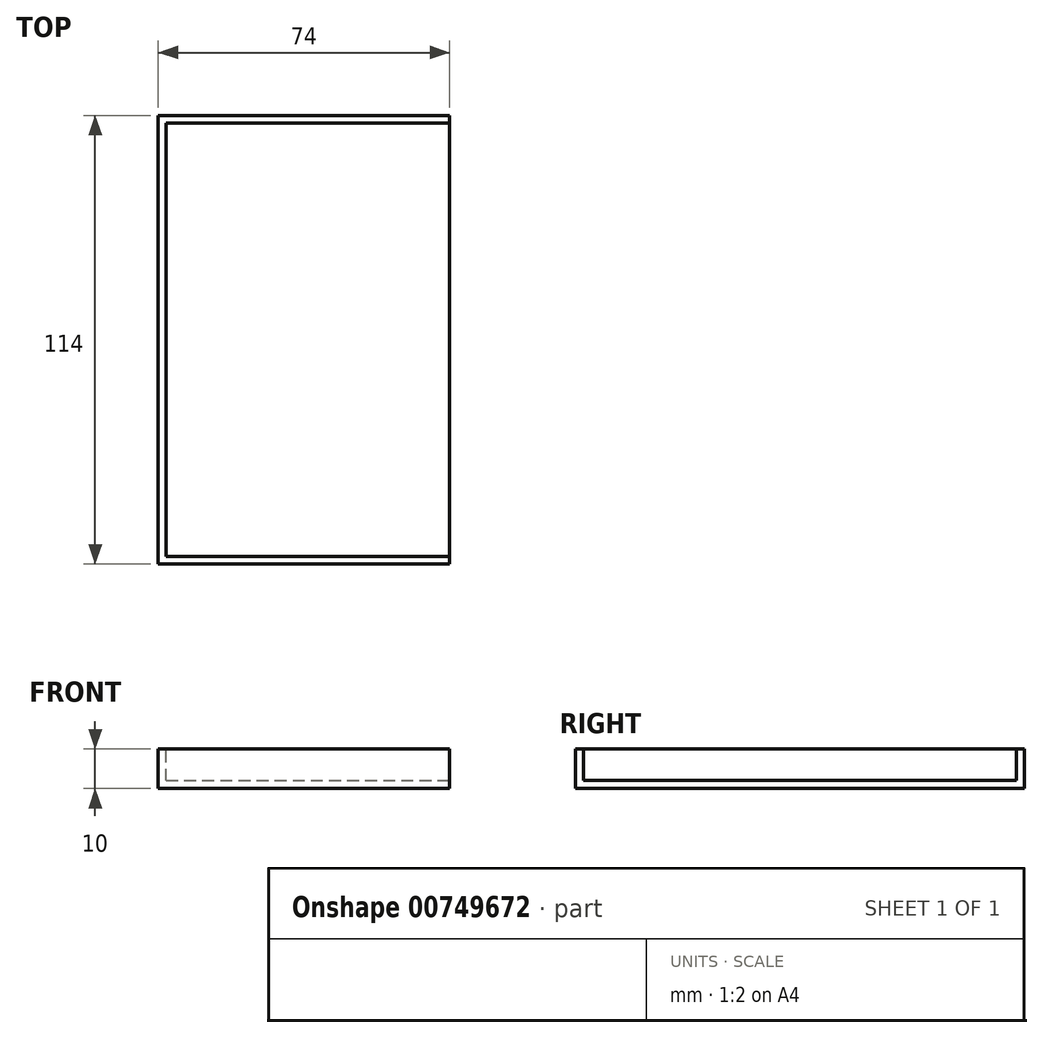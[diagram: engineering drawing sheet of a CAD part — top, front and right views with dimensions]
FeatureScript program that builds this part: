
annotation { "Feature Type Name" : "Feature", "Feature Type Description" : "" }
export const myFeature = defineFeature(function(context is Context, id is Id, definition is map)
    precondition{}
    {
        {
            var Q0;
            Q0=qCreatedBy(makeId("Top.planeOp"),FACE);
            var sketch = newSketch(context, id + "F0", { "sketchPlane" : qUnion([Q0])});
            skLineSegment(sketch, "E0.bottom", {"start": v(-89.45, 57) * mm, "end": v(-15.45, 57) * mm});
            skLineSegment(sketch, "E0.top", {"start": v(-89.45, -57) * mm, "end": v(-15.45, -57) * mm});
            skLineSegment(sketch, "E0.left", {"start": v(-89.45, 57) * mm, "end": v(-89.45, -57) * mm});
            skLineSegment(sketch, "E0.right", {"start": v(-15.45, 57) * mm, "end": v(-15.45, -57) * mm});
            skSolve(sketch);
        }
        {
            var Q0;
            Q0=qSketchRegion(id+"F0",true);
            extrude(context, id + "F1", {"entities" : qUnion([Q0]), "depth" : 10 * mm, "offsetDistance" : 25 * mm});
        }
        {
            var Q0;
            Q0=makeQuery(id+"F1.opExtrude","CAP_FACE",FACE,{"disambiguationData":[OSD([sQuery(id+"F0.wireOp",EDGE,"E0.bottom"),sQuery(id+"F0.wireOp",EDGE,"E0.top"),sQuery(id+"F0.wireOp",EDGE,"E0.left"),sQuery(id+"F0.wireOp",EDGE,"E0.right")])],"isStart":false});
            var sketch = newSketch(context, id + "F2", { "sketchPlane" : qUnion([Q0])});
            skLineSegment(sketch, "E1.0", {"start": v(-89.45, 57) * mm, "end": v(-15.45, 57) * mm, "construction": true});
            skLineSegment(sketch, "E1.1", {"start": v(-89.45, 57) * mm, "end": v(-89.45, -57) * mm, "construction": true});
            skLineSegment(sketch, "E1.2", {"start": v(-15.45, 57) * mm, "end": v(-15.45, -57) * mm, "construction": true});
            skLineSegment(sketch, "E1.3", {"start": v(-89.45, -57) * mm, "end": v(-15.45, -57) * mm, "construction": true});
            skLineSegment(sketch, "E2.bottom", {"start": v(-87.45, 55) * mm, "end": v(15.93, 55) * mm});
            skLineSegment(sketch, "E2.top", {"start": v(-87.45, -55) * mm, "end": v(15.93, -55) * mm});
            skLineSegment(sketch, "E2.left", {"start": v(-87.45, 55) * mm, "end": v(-87.45, -55) * mm});
            skLineSegment(sketch, "E2.right", {"start": v(15.93, 55) * mm, "end": v(15.93, -55) * mm});
            skSolve(sketch);
        }
        {
            var Q0;
            Q0=qSketchRegion(id+"F2",true);
            extrude(context, id + "F3", {"entities" : qUnion([Q0]), "operationType" : NewBodyOperationType.REMOVE, "oppositeDirection" : true, "depth" : 8 * mm, "offsetDistance" : 25 * mm});
        }
    });
